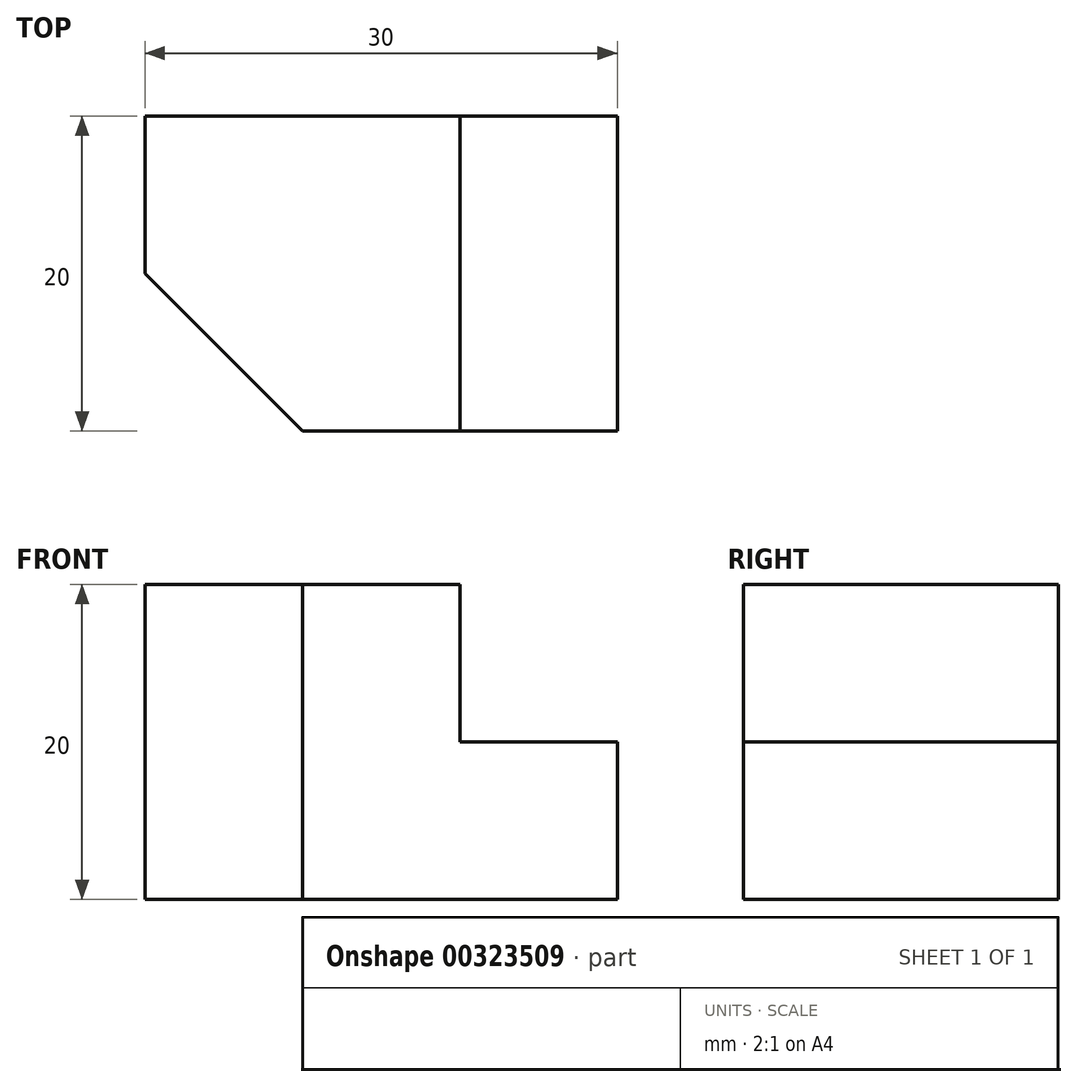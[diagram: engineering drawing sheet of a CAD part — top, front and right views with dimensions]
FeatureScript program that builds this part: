
annotation { "Feature Type Name" : "Feature", "Feature Type Description" : "" }
export const myFeature = defineFeature(function(context is Context, id is Id, definition is map)
    precondition{}
    {
        {
            var Q0;
            Q0=qCreatedBy(makeId("Top.planeOp"),FACE);
            var sketch = newSketch(context, id + "F0", { "sketchPlane" : qUnion([Q0])});
            skLineSegment(sketch, "E0", {"start": v(0, 0) * mm, "end": v(-10, 10) * mm});
            skLineSegment(sketch, "E1", {"start": v(-10, 10) * mm, "end": v(-10, 20) * mm});
            skLineSegment(sketch, "E2", {"start": v(-10, 20) * mm, "end": v(10, 20) * mm});
            skLineSegment(sketch, "E3", {"start": v(10, 20) * mm, "end": v(10, 0) * mm});
            skLineSegment(sketch, "E4", {"start": v(10, 0) * mm, "end": v(0, 0) * mm});
            skSolve(sketch);
        }
        {
            var Q0;
            Q0 = qSketchRegion(id + "F0", true);
            extrude(context, id + "F1", {"entities" : qUnion([Q0]), "depth" : 20 * mm});
        }
        {
            var Q0;
            Q0=makeQuery(id+"F1.opExtrude","SWEPT_FACE",FACE,{"disambiguationData":[OSD([sQuery(id+"F0.wireOp",EDGE,"E3")])]});
            var sketch = newSketch(context, id + "F2", { "sketchPlane" : qUnion([Q0])});
            skLineSegment(sketch, "E5", {"start": v(0, 0) * mm, "end": v(0, 10) * mm});
            skLineSegment(sketch, "E6", {"start": v(0, 10) * mm, "end": v(20, 10) * mm});
            skLineSegment(sketch, "E7", {"start": v(20, 10) * mm, "end": v(20, 0) * mm});
            skLineSegment(sketch, "E8", {"start": v(20, 0) * mm, "end": v(0, 0) * mm});
            skSolve(sketch);
        }
        {
            var Q0;
            Q0 = qSketchRegion(id + "F2", true);
            extrude(context, id + "F3", {"entities" : qUnion([Q0]), "operationType" : NewBodyOperationType.ADD, "depth" : 10 * mm});
        }
    });
